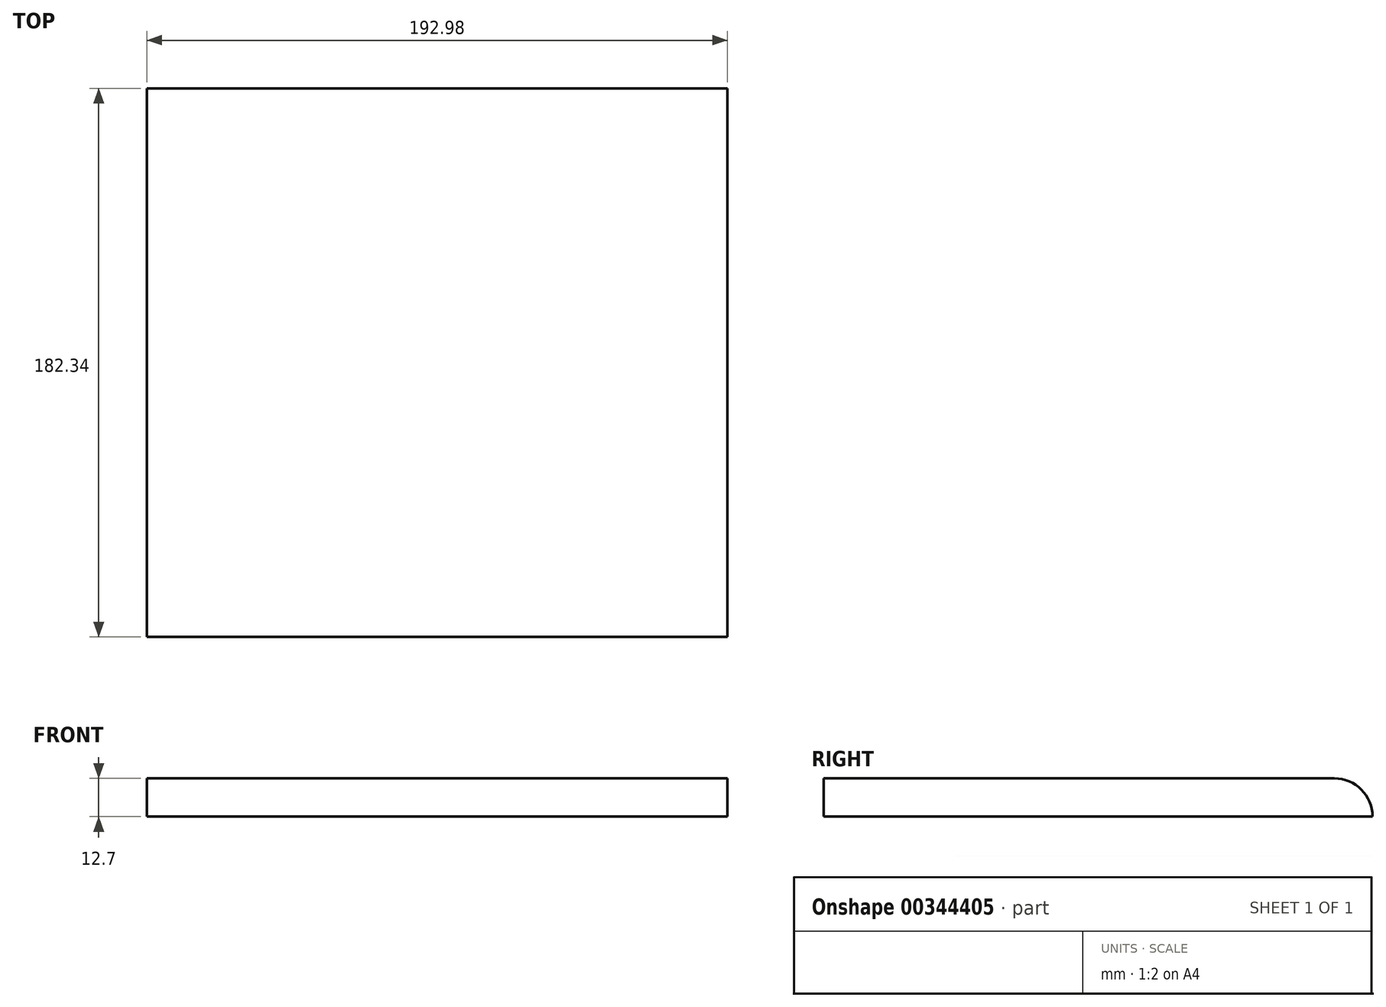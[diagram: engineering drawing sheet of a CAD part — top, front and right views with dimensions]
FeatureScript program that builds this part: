
annotation { "Feature Type Name" : "Feature", "Feature Type Description" : "" }
export const myFeature = defineFeature(function(context is Context, id is Id, definition is map)
    precondition{}
    {
        {
            var Q0;
            Q0=qCreatedBy(makeId("Top.planeOp"),FACE);
            var sketch = newSketch(context, id + "F0", { "sketchPlane" : qUnion([Q0])});
            skLineSegment(sketch, "E0.bottom", {"start": v(-96.49, -91.17) * mm, "end": v(96.49, -91.17) * mm});
            skLineSegment(sketch, "E0.top", {"start": v(-96.49, 91.17) * mm, "end": v(96.49, 91.17) * mm});
            skLineSegment(sketch, "E0.left", {"start": v(-96.49, -91.17) * mm, "end": v(-96.49, 91.17) * mm});
            skLineSegment(sketch, "E0.right", {"start": v(96.49, -91.17) * mm, "end": v(96.49, 91.17) * mm});
            skPoint(sketch, "E0.middle", {"position": v(0, 0) * mm});
            skSolve(sketch);
        }
        {
            var Q0;
            Q0=makeQuery(id+"F0.imprint","IMPRINT",FACE,{"disambiguationData":[TD([[makeQuery(id+"F0.imprint","IMPRINT",EDGE,{"derivedFrom":sQuery(id+"F0.wireOp",EDGE,"E0.bottom")}),1.0]])]});
            extrude(context, id + "F1", {"entities" : qUnion([Q0]), "depth" : 12.7 * mm});
        }
        {
            var Q0;
            Q0=qCreatedBy(makeId("Right.planeOp"),FACE);
            var sketch = newSketch(context, id + "F2", { "sketchPlane" : qUnion([Q0])});
            skFitSpline(sketch, "E1", {"points": [v(-86.74, 12.24) * mm, v(-98.4, 49.38) * mm, v(-110.55, 154.5) * mm], "startDerivative": vector(-31.8, 83.9) * mm, "endDerivative": vector(-16.22, 190.41) * mm});
            skSolve(sketch);
        }
        {
            var Q0;
            Q0 = qSketchRegion(id + "F2", true);
            var Q1;
            Q1=sQuery(id+"F2.wireOp",EDGE,"E1");
            extrude(context, id + "F3", {"entities" : qUnion([Q0]), "bodyType" : ToolBodyType.SURFACE, "surfaceEntities" : qUnion([Q1]), "endBound" : BoundingType.SYMMETRIC, "depth" : 193.04 * mm});
        }
        {
            var Q0;
            Q0=makeQuery(id+"F1.opExtrude","CAP_EDGE",EDGE,{"disambiguationData":[OSD([sQuery(id+"F0.wireOp",EDGE,"E0.top")])],"isStart":false});
            fillet(context, id + "F4", {"entities" : qUnion([Q0]), "radius" : 12.7 * mm, "tangentPropagation" : true, "allowEdgeOverflow" : false});
        }
    });
